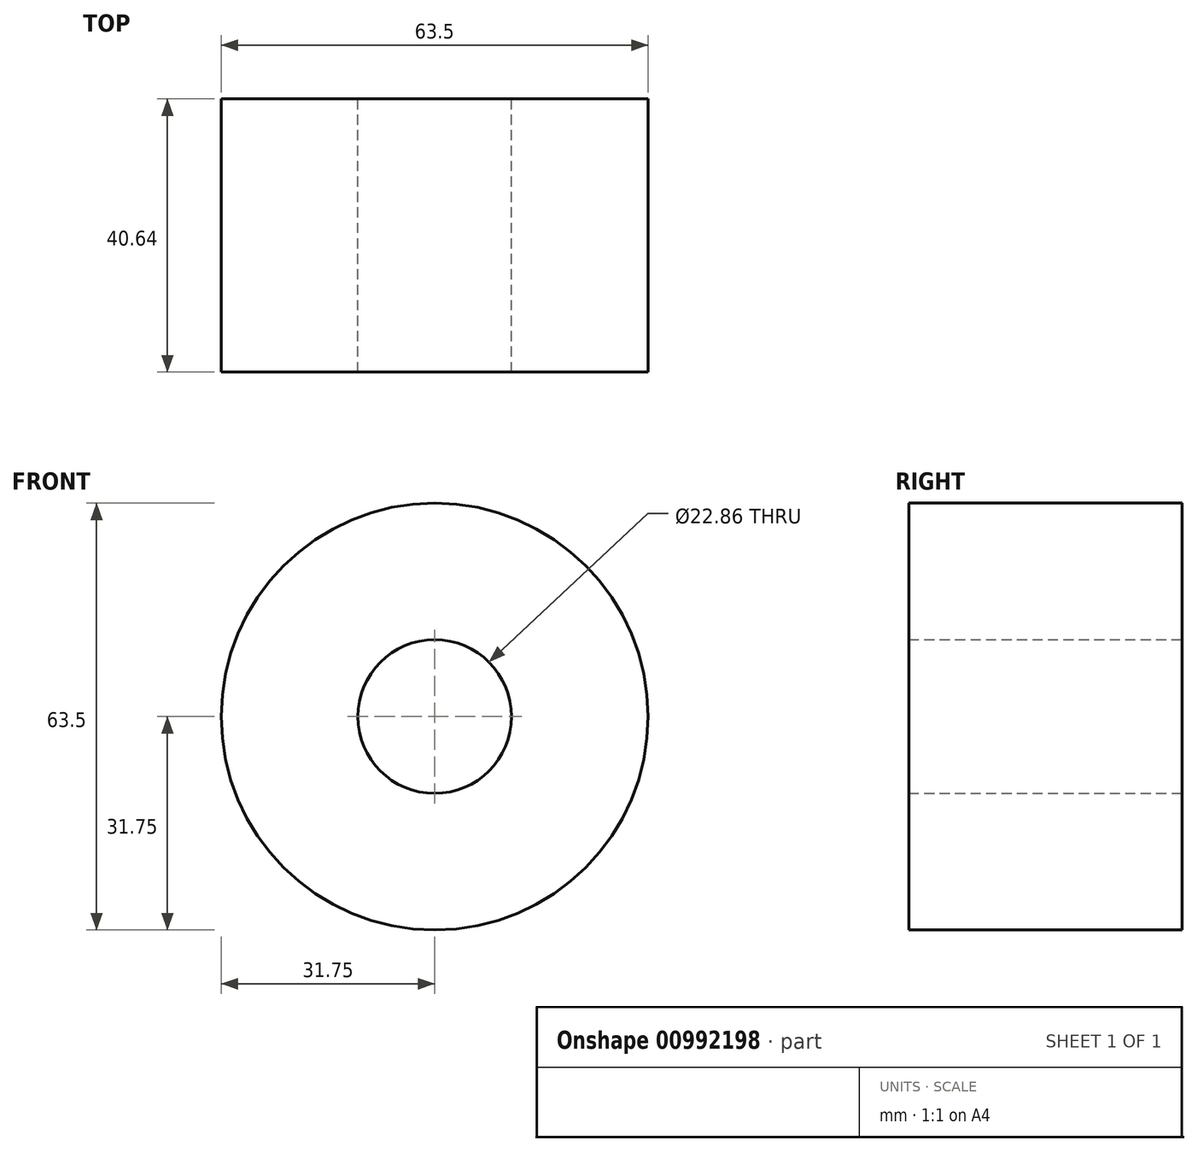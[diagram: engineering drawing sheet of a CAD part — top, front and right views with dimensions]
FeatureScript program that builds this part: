
annotation { "Feature Type Name" : "Feature", "Feature Type Description" : "" }
export const myFeature = defineFeature(function(context is Context, id is Id, definition is map)
    precondition{}
    {
        {
            var Q0;
            Q0=qCreatedBy(makeId("Front.planeOp"),FACE);
            var sketch = newSketch(context, id + "F0", { "sketchPlane" : qUnion([Q0])});
            skCircle(sketch, "E0", {"center": v(0, 0) * mm, "radius": 31.75 * mm});
            skCircle(sketch, "E1", {"center": v(0, 0) * mm, "radius": 11.43 * mm});
            skSolve(sketch);
        }
        {
            var Q0;
            Q0=makeQuery(id+"F0.imprint","IMPRINT",FACE,{"disambiguationData":[TD([[makeQuery(id+"F0.imprint","IMPRINT",EDGE,{"derivedFrom":sQuery(id+"F0.wireOp",EDGE,"E0")}),1.0]])]});
            extrude(context, id + "F1", {"entities" : qUnion([Q0]), "depth" : 40.64 * mm, "offsetDistance" : 25.4 * mm});
        }
    });
